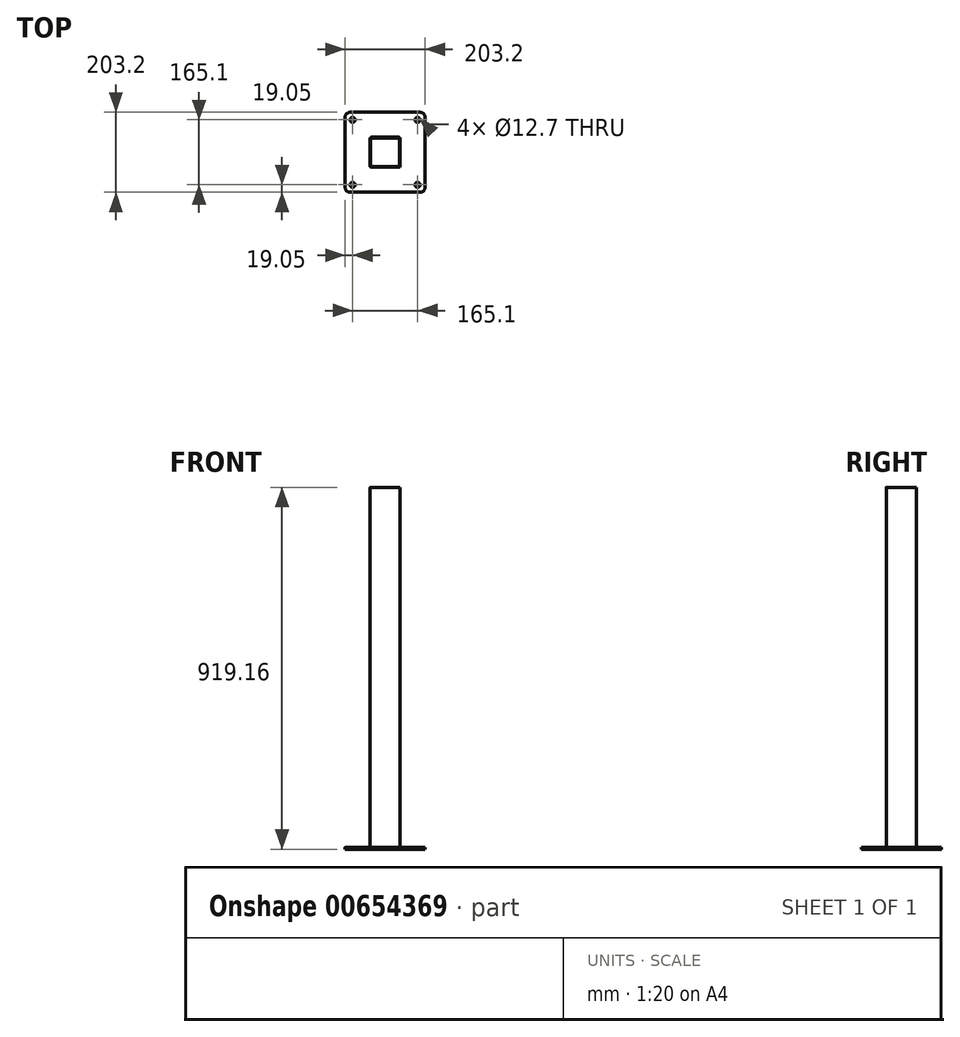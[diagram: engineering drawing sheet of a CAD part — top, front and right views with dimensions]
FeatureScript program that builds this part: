
annotation { "Feature Type Name" : "Feature", "Feature Type Description" : "" }
export const myFeature = defineFeature(function(context is Context, id is Id, definition is map)
    precondition{}
    {
        {
            var Q0;
            Q0=qCreatedBy(makeId("Top.planeOp"),FACE);
            var sketch = newSketch(context, id + "F0", { "sketchPlane" : qUnion([Q0])});
            skLineSegment(sketch, "E0.bottom", {"start": v(-101.6, 101.6) * mm, "end": v(101.6, 101.6) * mm});
            skLineSegment(sketch, "E0.top", {"start": v(-101.6, -101.6) * mm, "end": v(101.6, -101.6) * mm});
            skLineSegment(sketch, "E0.left", {"start": v(-101.6, 101.6) * mm, "end": v(-101.6, -101.6) * mm});
            skLineSegment(sketch, "E0.right", {"start": v(101.6, 101.6) * mm, "end": v(101.6, -101.6) * mm});
            skPoint(sketch, "E0.middle", {"position": v(0, 0) * mm});
            skCircle(sketch, "E1", {"center": v(-82.55, -82.55) * mm, "radius": 6.35 * mm});
            skCircle(sketch, "E2.0.1.0", {"center": v(-82.55, 82.55) * mm, "radius": 6.35 * mm});
            skCircle(sketch, "E2.1.0.0", {"center": v(82.55, -82.55) * mm, "radius": 6.35 * mm});
            skCircle(sketch, "E2.1.1.0", {"center": v(82.55, 82.55) * mm, "radius": 6.35 * mm});
            skLineSegment(sketch, "E2.direction1", {"start": v(-82.55, -82.55) * mm, "end": v(82.55, -82.55) * mm, "construction": true});
            skLineSegment(sketch, "E2.direction2", {"start": v(-82.55, -82.55) * mm, "end": v(-82.55, 82.55) * mm, "construction": true});
            skSolve(sketch);
        }
        {
            var Q0;
            Q0=makeQuery(id+"F0.imprint","IMPRINT",FACE,{"disambiguationData":[TD([[makeQuery(id+"F0.imprint","IMPRINT",EDGE,{"derivedFrom":sQuery(id+"F0.wireOp",EDGE,"E0.bottom")}),-1.0]])]});
            extrude(context, id + "F1", {"entities" : qUnion([Q0]), "depth" : 4.76 * mm, "offsetDistance" : 25.4 * mm});
        }
        {
            var Q0;
            Q0=makeQuery(id+"F1.opExtrude","SWEPT_EDGE",EDGE,{"disambiguationData":[OSD([sQuery(id+"F0.wireOp",EDGE,"E0.top"),sQuery(id+"F0.wireOp",EDGE,"E0.left")])]});
            var Q1;
            Q1=makeQuery(id+"F1.opExtrude","SWEPT_EDGE",EDGE,{"disambiguationData":[OSD([sQuery(id+"F0.wireOp",EDGE,"E0.top"),sQuery(id+"F0.wireOp",EDGE,"E0.right")])]});
            var Q2;
            Q2=makeQuery(id+"F1.opExtrude","SWEPT_EDGE",EDGE,{"disambiguationData":[OSD([sQuery(id+"F0.wireOp",EDGE,"E0.bottom"),sQuery(id+"F0.wireOp",EDGE,"E0.right")])]});
            var Q3;
            Q3=makeQuery(id+"F1.opExtrude","SWEPT_EDGE",EDGE,{"disambiguationData":[OSD([sQuery(id+"F0.wireOp",EDGE,"E0.bottom"),sQuery(id+"F0.wireOp",EDGE,"E0.left")])]});
            fillet(context, id + "F2", {"entities" : qUnion([Q0, Q1, Q2, Q3]), "radius" : 12.7 * mm, "tangentPropagation" : true, "allowEdgeOverflow" : false});
        }
        {
            var Q0;
            Q0=makeQuery(id+"F1.opExtrude","CAP_FACE",FACE,{"disambiguationData":[OSD([sQuery(id+"F0.wireOp",EDGE,"E0.bottom"),sQuery(id+"F0.wireOp",EDGE,"E0.top"),sQuery(id+"F0.wireOp",EDGE,"E0.left"),sQuery(id+"F0.wireOp",EDGE,"E0.right"),sQuery(id+"F0.wireOp",EDGE,"E1"),sQuery(id+"F0.wireOp",EDGE,"E2.0.1.0"),sQuery(id+"F0.wireOp",EDGE,"E2.1.0.0"),sQuery(id+"F0.wireOp",EDGE,"E2.1.1.0")])],"isStart":false});
            var sketch = newSketch(context, id + "F3", { "sketchPlane" : qUnion([Q0])});
            skLineSegment(sketch, "E3.bottom", {"start": v(-34.92, 38.1) * mm, "end": v(34.93, 38.1) * mm});
            skLineSegment(sketch, "E3.top", {"start": v(-34.93, -38.1) * mm, "end": v(34.92, -38.1) * mm});
            skLineSegment(sketch, "E3.left", {"start": v(-38.1, 34.93) * mm, "end": v(-38.1, -34.93) * mm});
            skLineSegment(sketch, "E3.right", {"start": v(38.1, 34.93) * mm, "end": v(38.1, -34.93) * mm});
            skPoint(sketch, "E3.middle", {"position": v(0, 0) * mm});
            skPoint(sketch, "E4.visualSharp", {"position": v(-38.1, 38.1) * mm});
            skArc(sketch, "E4.filletArc", {"start": v(-34.92, 38.1) * mm, "mid": v(-37.17, 37.17) * mm, "end": v(-38.1, 34.93) * mm});
            skPoint(sketch, "E5.visualSharp", {"position": v(38.1, 38.1) * mm});
            skArc(sketch, "E5.filletArc", {"start": v(38.1, 34.93) * mm, "mid": v(37.17, 37.17) * mm, "end": v(34.93, 38.1) * mm});
            skPoint(sketch, "E6.visualSharp", {"position": v(38.1, -38.1) * mm});
            skArc(sketch, "E6.filletArc", {"start": v(34.92, -38.1) * mm, "mid": v(37.17, -37.17) * mm, "end": v(38.1, -34.93) * mm});
            skPoint(sketch, "E7.visualSharp", {"position": v(-38.1, -38.1) * mm});
            skArc(sketch, "E7.filletArc", {"start": v(-38.1, -34.93) * mm, "mid": v(-37.17, -37.17) * mm, "end": v(-34.93, -38.1) * mm});
            skLineSegment(sketch, "E8.0", {"start": v(-36.51, 34.93) * mm, "end": v(-36.51, -34.93) * mm});
            skLineSegment(sketch, "E9.0", {"start": v(-34.92, 36.51) * mm, "end": v(34.93, 36.51) * mm});
            skLineSegment(sketch, "E10.0", {"start": v(36.51, 34.93) * mm, "end": v(36.51, -34.93) * mm});
            skLineSegment(sketch, "E11.0", {"start": v(-34.93, -36.51) * mm, "end": v(34.92, -36.51) * mm});
            skArc(sketch, "E12", {"start": v(-36.51, -34.93) * mm, "mid": v(-36.05, -36.05) * mm, "end": v(-34.93, -36.51) * mm});
            skArc(sketch, "E13", {"start": v(-34.92, 36.51) * mm, "mid": v(-36.05, 36.05) * mm, "end": v(-36.51, 34.93) * mm});
            skArc(sketch, "E14", {"start": v(36.51, 34.93) * mm, "mid": v(36.05, 36.05) * mm, "end": v(34.93, 36.51) * mm});
            skArc(sketch, "E15", {"start": v(34.92, -36.51) * mm, "mid": v(36.05, -36.05) * mm, "end": v(36.51, -34.93) * mm});
            skSolve(sketch);
        }
        {
            var Q0;
            Q0=makeQuery(id+"F3.imprint","IMPRINT",FACE,{"disambiguationData":[TD([[makeQuery(id+"F3.imprint","IMPRINT",EDGE,{"derivedFrom":sQuery(id+"F3.wireOp",EDGE,"E3.bottom")}),-1.0]])]});
            extrude(context, id + "F4", {"entities" : qUnion([Q0]), "operationType" : NewBodyOperationType.ADD, "depth" : 914.4 * mm, "offsetDistance" : 25.4 * mm});
        }
    });
